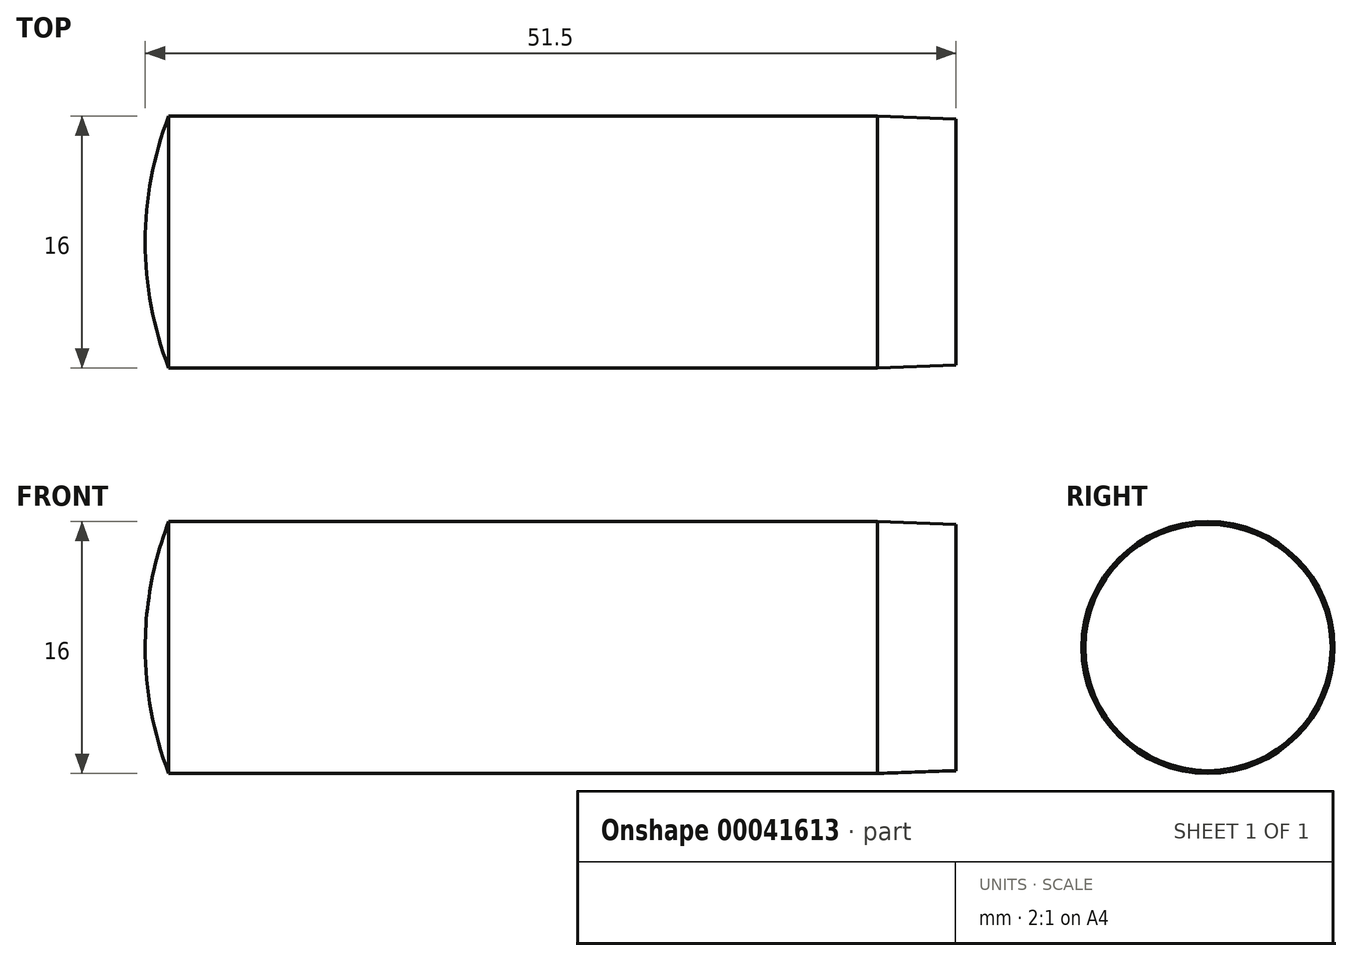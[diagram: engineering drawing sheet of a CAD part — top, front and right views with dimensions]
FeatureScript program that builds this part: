
annotation { "Feature Type Name" : "Feature", "Feature Type Description" : "" }
export const myFeature = defineFeature(function(context is Context, id is Id, definition is map)
    precondition{}
    {
        {
            var Q0;
            Q0=qCreatedBy(makeId("Front.planeOp"),FACE);
            var sketch = newSketch(context, id + "F0", { "sketchPlane" : qUnion([Q0])});
            skLineSegment(sketch, "E0.rect.bottom", {"start": v(50, 8) * mm, "end": v(0, 8) * mm});
            skLineSegment(sketch, "E0.rect.top", {"start": v(50, -8) * mm, "end": v(0, -8) * mm, "construction": true});
            skLineSegment(sketch, "E0.rect.left", {"start": v(50, 8) * mm, "end": v(50, -8) * mm, "construction": true});
            skLineSegment(sketch, "E0.rect.right", {"start": v(0, 8) * mm, "end": v(0, -8) * mm, "construction": true});
            skPoint(sketch, "E0.rect.middle", {"position": v(25, 0) * mm});
            skLineSegment(sketch, "E1", {"start": v(0, 0) * mm, "end": v(50, 0) * mm});
            skLineSegment(sketch, "E2", {"start": v(0, 8) * mm, "end": v(0, 0) * mm, "construction": true});
            skLineSegment(sketch, "E3", {"start": v(50, 8) * mm, "end": v(50, 0) * mm});
            skLineSegment(sketch, "E4", {"start": v(0, 0) * mm, "end": v(-1.5, 0) * mm});
            skArc(sketch, "E5", {"start": v(0, 8) * mm, "mid": v(-1.12, 4.07) * mm, "end": v(-1.5, 0) * mm});
            skLineSegment(sketch, "E6", {"start": v(-1.5, 0) * mm, "end": v(50, 0) * mm});
            skSolve(sketch);
        }
        {
            var Q0;
            Q0=makeQuery(id+"F0.imprint","IMPRINT",FACE,{"disambiguationData":[TD([[makeQuery(id+"F0.imprint","IMPRINT",EDGE,{"derivedFrom":sQuery(id+"F0.wireOp",EDGE,"E0.rect.bottom")}),1.0]])]});
            var Q1;
            Q1=sQuery(id+"F0.wireOp",EDGE,"E6");
            revolve(context, id + "F1", {"entities" : qUnion([Q0]), "axis" : qUnion([Q1]), "revolveType" : RevolveType.FULL});
        }
        {
            var Q0;
            Q0=makeQuery(id+"F1.opRevolve","SWEPT_EDGE",EDGE,{"disambiguationData":[OSD([sQuery(id+"F0.wireOp",EDGE,"E0.rect.bottom"),sQuery(id+"F0.wireOp",EDGE,"E3")])]});
            chamfer(context, id + "F2", {"entities" : qUnion([Q0]), "chamferType" : ChamferType.OFFSET_ANGLE, "width" : 5 * mm, "oppositeDirection" : false, "angle" : 2 * degree, "tangentPropagation" : true});
        }
    });
